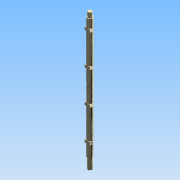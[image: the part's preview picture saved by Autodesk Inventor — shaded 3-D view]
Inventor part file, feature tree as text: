
AUTODESK INVENTOR PART (.ipt)
format: ipt  version: 2015 (Build 190159000, 159)  size: 126,464 bytes
history: native  units: mm
features: extrude x5, sketch x5, chamfer x1, plane x1, pattern_linear x1
ambient origin geometry x8: Origin, YZ Plane, XZ Plane, XY Plane, X Axis, Y Axis, Z Axis, Center Point
bodies: 实体1 (feature_tree)
feature tree (13):
  extrude  "拉伸1"  Depth=447.0mm TaperAngle=0.0deg
  extrude  "拉伸2"  Depth=18.0mm TaperAngle=0.0deg
  chamfer  "倒角1"  Distance=1.0mm Angle=45.0deg
  extrude  "拉伸3"  Depth=40.0mm TaperAngle=0.0deg
  plane  "工作平面1"
  extrude  "拉伸4"  Depth=20.0mm
  pattern_linear  "矩形阵列1"  Count1=2  [1 undecoded]
  extrude  "拉伸5"  Depth=10.0mm
  sketch  "草图1"  dims[d0=20.0mm d1=447.0mm d2=0.0mm]
  sketch  "草图2"  dims[d3=15.0mm d4=18.0mm d5=0.0mm d6=1.0mm d7=2.0mm d8=45.0deg]
  sketch  "草图3"  dims[d9=15.0mm d10=40.0mm d11=0.0mm]
  sketch  "草图4"  dims[d12=-45.0mm d13=20.0mm d14=20.0mm]
  sketch  "草图5"  dims[d15=10.0mm d16=10.0mm d17=10.0mm d18=0.0mm d19=40.0mm d21=120.0mm d22=15.0mm d23=10.0mm d24=9.773844mm d25=20.0mm d26=0.0mm]
note: 1 required parameter value undecoded (feature->parameter linkage not recoverable at this tier; creation-order binding heuristic only, values carry confidence <= 0.55)
